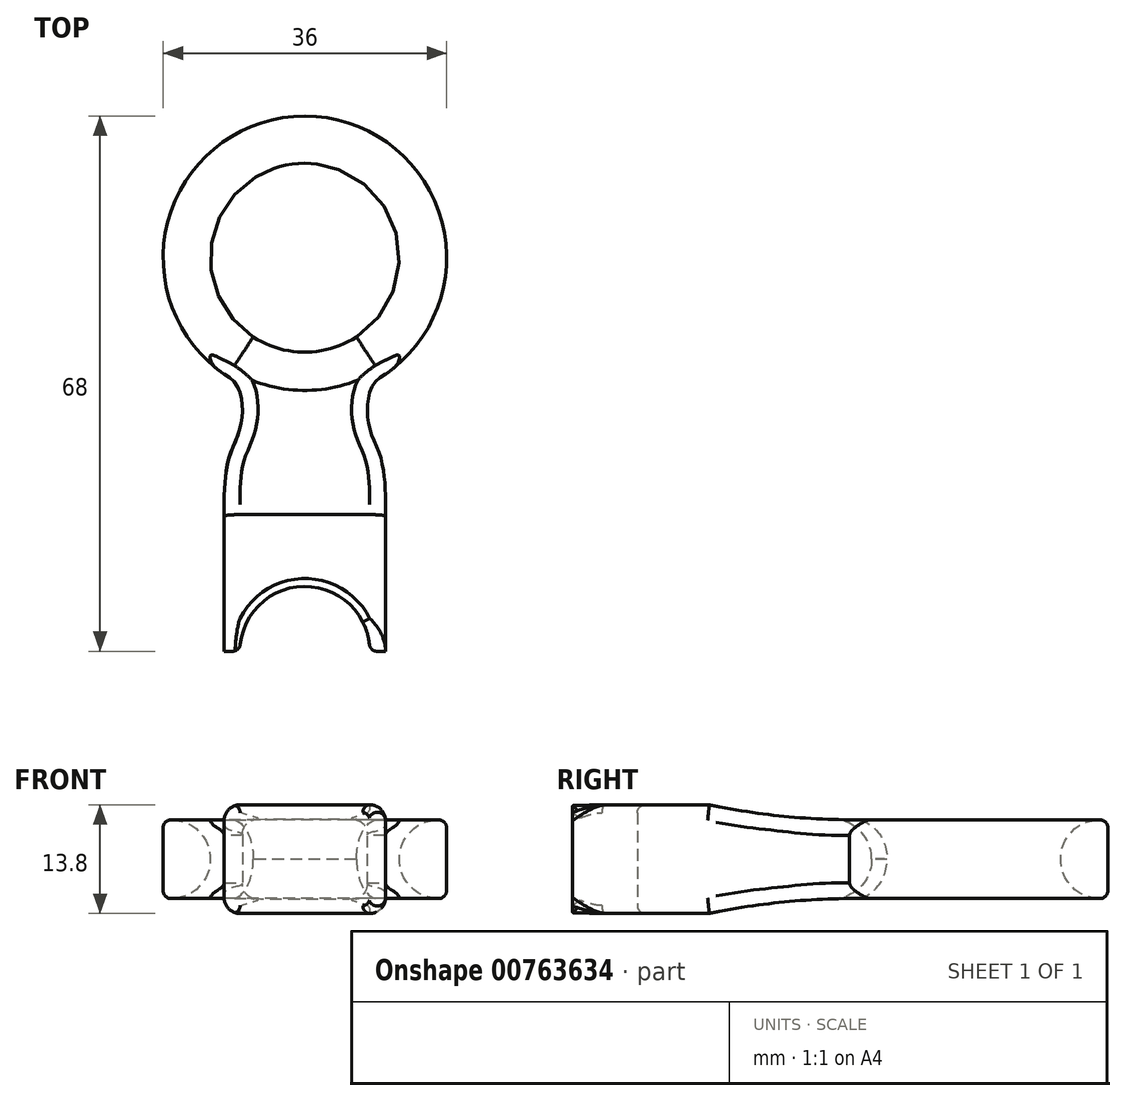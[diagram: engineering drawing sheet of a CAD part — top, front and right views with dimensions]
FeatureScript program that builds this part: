
annotation { "Feature Type Name" : "Feature", "Feature Type Description" : "" }
export const myFeature = defineFeature(function(context is Context, id is Id, definition is map)
    precondition{}
    {
        {
            var Q0;
            Q0=qCreatedBy(makeId("Top.planeOp"),FACE);
            var sketch = newSketch(context, id + "F0", { "sketchPlane" : qUnion([Q0])});
            skLineSegment(sketch, "E0.top", {"start": v(-10.25, 18.25) * mm, "end": v(10.25, 18.25) * mm, "construction": true});
            skLineSegment(sketch, "E0.left", {"start": v(-10.25, 0) * mm, "end": v(-10.25, 18.25) * mm});
            skLineSegment(sketch, "E0.right", {"start": v(10.25, 0) * mm, "end": v(10.25, 18.25) * mm});
            skLineSegment(sketch, "E1", {"start": v(-10.25, 0) * mm, "end": v(-8.25, 0) * mm});
            skLineSegment(sketch, "E2", {"start": v(10.25, 0) * mm, "end": v(8.25, 0) * mm});
            skArc(sketch, "E3", {"start": v(8.25, 0) * mm, "mid": v(0, 8.25) * mm, "end": v(-8.25, 0) * mm});
            skLineSegment(sketch, "E4", {"start": v(-18.15, 8.25) * mm, "end": v(25.8, 8.25) * mm, "construction": true});
            skFitSpline(sketch, "E5", {"points": [v(-10.25, 18.25) * mm, v(-8.27, 28.22) * mm, v(-10.25, 35.2) * mm], "startDerivative": vector(-0.23, 39.15) * mm, "endDerivative": vector(-17.29, 7.4) * mm});
            skFitSpline(sketch, "E6.MirrorCS", {"points": [v(10.25, 18.25) * mm, v(8.27, 28.22) * mm, v(10.25, 35.2) * mm], "startDerivative": vector(0.23, 39.15) * mm, "endDerivative": vector(17.29, 7.4) * mm});
            skArc(sketch, "E7", {"start": v(10.25, 35.2) * mm, "mid": v(0, 68) * mm, "end": v(-10.25, 35.2) * mm});
            skCircle(sketch, "E8", {"center": v(0, 50) * mm, "radius": 12 * mm});
            skSolve(sketch);
        }
        {
            var Q0;
            Q0=makeQuery(id+"F0.imprint","IMPRINT",FACE,{"disambiguationData":[TD([[makeQuery(id+"F0.imprint","IMPRINT",EDGE,{"derivedFrom":sQuery(id+"F0.wireOp",EDGE,"E0.left")}),-1.0]])]});
            extrude(context, id + "F1", {"entities" : qUnion([Q0]), "depth" : 13.8 * mm, "offsetDistance" : 25 * mm});
        }
        {
            var Q0;
            Q0=qCreatedBy(makeId("Right.planeOp"),FACE);
            var sketch = newSketch(context, id + "F2", { "sketchPlane" : qUnion([Q0])});
            skLineSegment(sketch, "E9", {"start": v(68, 11.9) * mm, "end": v(35.76, 11.9) * mm});
            skLineSegment(sketch, "E10", {"start": v(17.37, 13.8) * mm, "end": v(68, 13.8) * mm});
            skLineSegment(sketch, "E11", {"start": v(68, 13.8) * mm, "end": v(68, 11.9) * mm});
            skLineSegment(sketch, "E12", {"start": v(80.15, 6.9) * mm, "end": v(-3.68, 6.9) * mm, "construction": true});
            skArc(sketch, "E13", {"start": v(17.37, 13.8) * mm, "mid": v(26.51, 12.38) * mm, "end": v(35.76, 11.9) * mm});
            skLineSegment(sketch, "E14.MirrorCS", {"start": v(68, 1.9) * mm, "end": v(35.76, 1.9) * mm});
            skArc(sketch, "E15.MirrorCS", {"start": v(17.37, 0) * mm, "mid": v(26.51, 1.42) * mm, "end": v(35.76, 1.9) * mm});
            skLineSegment(sketch, "E16.MirrorCS", {"start": v(17.37, 0) * mm, "end": v(68, 0) * mm});
            skLineSegment(sketch, "E17.MirrorCS", {"start": v(68, 0) * mm, "end": v(68, 1.9) * mm});
            skSolve(sketch);
        }
        {
            var Q0;
            Q0 = qSketchRegion(id + "F2", true);
            extrude(context, id + "F3", {"entities" : qUnion([Q0]), "operationType" : NewBodyOperationType.REMOVE, "endBound" : BoundingType.SYMMETRIC, "oppositeDirection" : true, "depth" : 60 * mm, "offsetDistance" : 25 * mm});
        }
        {
            var Q0;
            Q0=makeQuery(id+"F3.boolean.opBoolean","INTERSECT",EDGE,{"derivedFrom":[makeQuery(id+"F1.opExtrude","SWEPT_FACE",FACE,{"disambiguationData":[OSD([sQuery(id+"F0.wireOp",EDGE,"E8")])]}),makeQuery(id+"F3.opExtrude","SWEPT_FACE",FACE,{"disambiguationData":[OSD([sQuery(id+"F2.wireOp",EDGE,"E9")])]})]});
            var Q1;
            Q1=makeQuery(id+"F3.boolean.opBoolean","INTERSECT",EDGE,{"derivedFrom":[makeQuery(id+"F1.opExtrude","SWEPT_FACE",FACE,{"disambiguationData":[OSD([sQuery(id+"F0.wireOp",EDGE,"E8")])]}),makeQuery(id+"F3.opExtrude","SWEPT_FACE",FACE,{"disambiguationData":[OSD([sQuery(id+"F2.wireOp",EDGE,"E14.MirrorCS")])]})]});
            fillet(context, id + "F4", {"entities" : qUnion([Q0, Q1]), "radius" : 5 * mm, "tangentPropagation" : true, "allowEdgeOverflow" : false});
        }
        {
            var Q0;
            Q0=makeQuery(id+"F3.boolean.opBoolean","INTERSECT",EDGE,{"derivedFrom":[makeQuery(id+"F1.opExtrude","SWEPT_FACE",FACE,{"disambiguationData":[OSD([sQuery(id+"F0.wireOp",EDGE,"E6.MirrorCS")])]}),makeQuery(id+"F3.opExtrude","SWEPT_FACE",FACE,{"disambiguationData":[OSD([sQuery(id+"F2.wireOp",EDGE,"E15.MirrorCS")])]})]});
            var Q1;
            Q1=makeQuery(id+"F1.opExtrude","CAP_EDGE",EDGE,{"disambiguationData":[OSD([sQuery(id+"F0.wireOp",EDGE,"E0.right")])],"isStart":true});
            var Q2;
            Q2=makeQuery(id+"F3.boolean.opBoolean","INTERSECT",EDGE,{"derivedFrom":[makeQuery(id+"F1.opExtrude","SWEPT_FACE",FACE,{"disambiguationData":[OSD([sQuery(id+"F0.wireOp",EDGE,"E5")])]}),makeQuery(id+"F3.opExtrude","SWEPT_FACE",FACE,{"disambiguationData":[OSD([sQuery(id+"F2.wireOp",EDGE,"E15.MirrorCS")])]})]});
            var Q3;
            Q3=makeQuery(id+"F1.opExtrude","CAP_EDGE",EDGE,{"disambiguationData":[OSD([sQuery(id+"F0.wireOp",EDGE,"E0.left")])],"isStart":true});
            var Q4;
            Q4=makeQuery(id+"F3.boolean.opBoolean","INTERSECT",EDGE,{"derivedFrom":[makeQuery(id+"F1.opExtrude","SWEPT_FACE",FACE,{"disambiguationData":[OSD([sQuery(id+"F0.wireOp",EDGE,"E6.MirrorCS")])]}),makeQuery(id+"F3.opExtrude","SWEPT_FACE",FACE,{"disambiguationData":[OSD([sQuery(id+"F2.wireOp",EDGE,"E13")])]})]});
            var Q5;
            Q5=makeQuery(id+"F1.opExtrude","CAP_EDGE",EDGE,{"disambiguationData":[OSD([sQuery(id+"F0.wireOp",EDGE,"E0.right")])],"isStart":false});
            var Q6;
            Q6=makeQuery(id+"F3.boolean.opBoolean","INTERSECT",EDGE,{"derivedFrom":[makeQuery(id+"F1.opExtrude","SWEPT_FACE",FACE,{"disambiguationData":[OSD([sQuery(id+"F0.wireOp",EDGE,"E5")])]}),makeQuery(id+"F3.opExtrude","SWEPT_FACE",FACE,{"disambiguationData":[OSD([sQuery(id+"F2.wireOp",EDGE,"E13")])]})]});
            var Q7;
            Q7=makeQuery(id+"F1.opExtrude","CAP_EDGE",EDGE,{"disambiguationData":[OSD([sQuery(id+"F0.wireOp",EDGE,"E0.left")])],"isStart":false});
            fillet(context, id + "F5", {"entities" : qUnion([Q0, Q1, Q2, Q3, Q4, Q5, Q6, Q7]), "radius" : 2 * mm, "tangentPropagation" : true, "allowEdgeOverflow" : false});
        }
        {
            var Q0;
            Q0=makeQuery(id+"F3.boolean.opBoolean","INTERSECT",EDGE,{"derivedFrom":[makeQuery(id+"F1.opExtrude","SWEPT_FACE",FACE,{"disambiguationData":[OSD([sQuery(id+"F0.wireOp",EDGE,"E7")])]}),makeQuery(id+"F3.opExtrude","SWEPT_FACE",FACE,{"disambiguationData":[OSD([sQuery(id+"F2.wireOp",EDGE,"E9")])]})]});
            var Q1;
            Q1=makeQuery(id+"F3.boolean.opBoolean","INTERSECT",EDGE,{"derivedFrom":[makeQuery(id+"F1.opExtrude","SWEPT_FACE",FACE,{"disambiguationData":[OSD([sQuery(id+"F0.wireOp",EDGE,"E7")])]}),makeQuery(id+"F3.opExtrude","SWEPT_FACE",FACE,{"disambiguationData":[OSD([sQuery(id+"F2.wireOp",EDGE,"E14.MirrorCS")])]})]});
            fillet(context, id + "F6", {"entities" : qUnion([Q0, Q1]), "radius" : 1 * mm, "tangentPropagation" : true, "allowEdgeOverflow" : false});
        }
        {
            var Q0;
            Q0=makeQuery(id+"F1.opExtrude","CAP_EDGE",EDGE,{"disambiguationData":[OSD([sQuery(id+"F0.wireOp",EDGE,"E3")])],"isStart":false});
            var Q1;
            Q1=makeQuery(id+"F1.opExtrude","CAP_EDGE",EDGE,{"disambiguationData":[OSD([sQuery(id+"F0.wireOp",EDGE,"E3")])],"isStart":true});
            var Q2;
            Q2=makeQuery(id+"F1.opExtrude","SWEPT_EDGE",EDGE,{"disambiguationData":[OSD([sQuery(id+"F0.wireOp",EDGE,"E1"),sQuery(id+"F0.wireOp",EDGE,"E3")])]});
            var Q3;
            Q3=makeQuery(id+"F1.opExtrude","SWEPT_EDGE",EDGE,{"disambiguationData":[OSD([sQuery(id+"F0.wireOp",EDGE,"E2"),sQuery(id+"F0.wireOp",EDGE,"E3")])]});
            fillet(context, id + "F7", {"entities" : qUnion([Q0, Q1, Q2, Q3]), "radius" : 1 * mm, "tangentPropagation" : true, "allowEdgeOverflow" : false});
        }
    });
